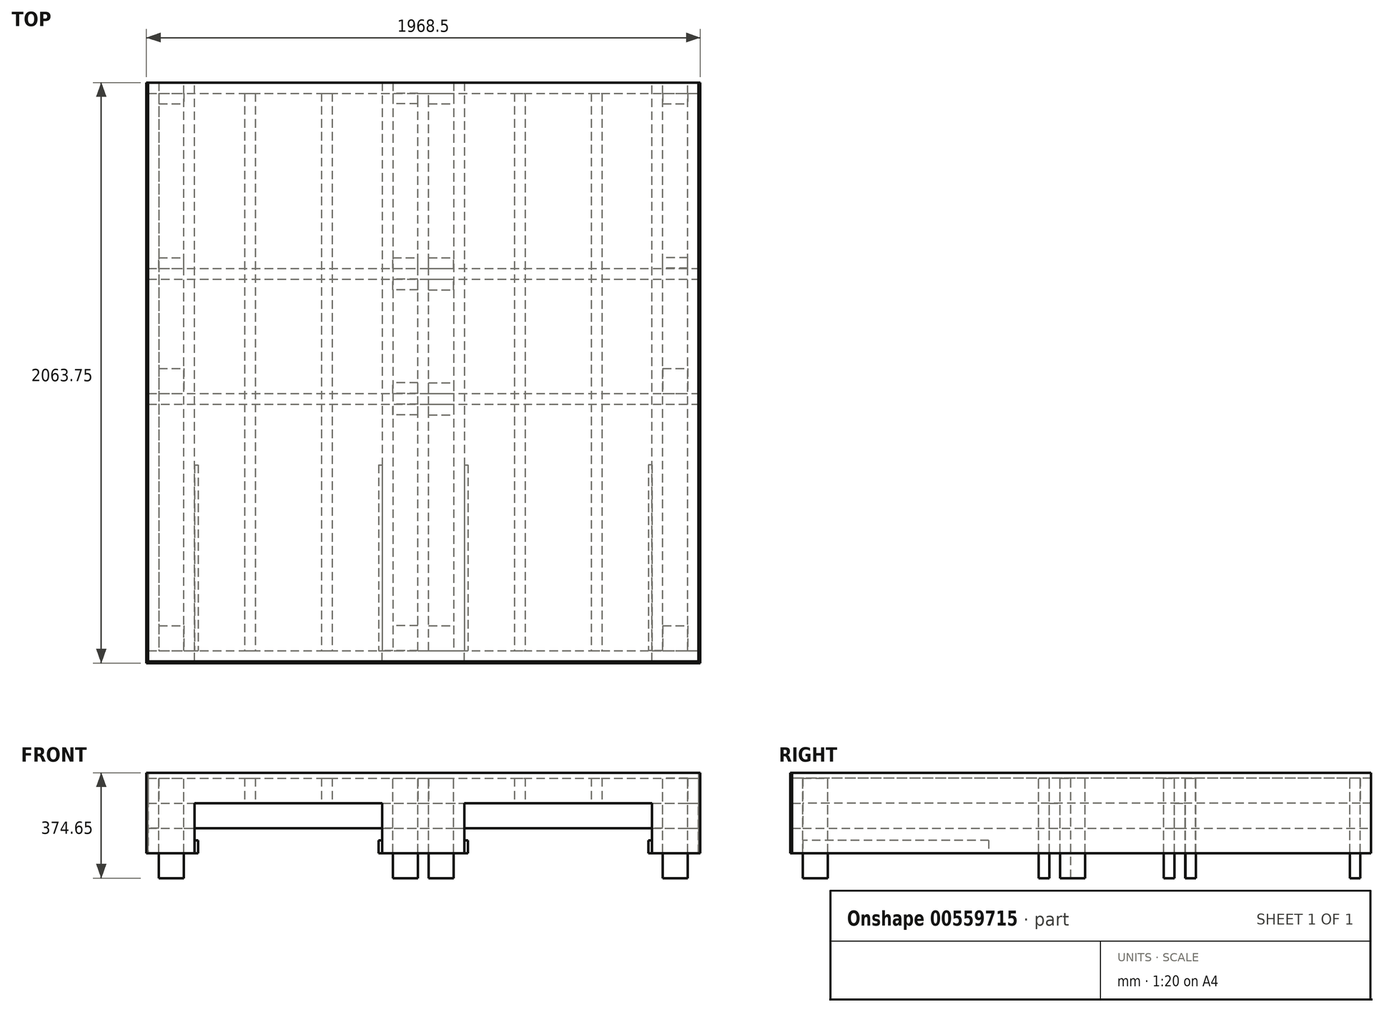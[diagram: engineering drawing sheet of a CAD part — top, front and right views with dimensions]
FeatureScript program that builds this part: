
annotation { "Feature Type Name" : "Feature", "Feature Type Description" : "" }
export const myFeature = defineFeature(function(context is Context, id is Id, definition is map)
    precondition{}
    {
        {
            var Q0;
            Q0=qCreatedBy(makeId("Top.planeOp"),FACE);
            var sketch = newSketch(context, id + "F0", { "sketchPlane" : qUnion([Q0])});
            skLineSegment(sketch, "E0.bottom", {"start": v(-977.9, 1981.2) * mm, "end": v(-939.8, 1981.2) * mm});
            skLineSegment(sketch, "E0.top", {"start": v(-977.9, 0) * mm, "end": v(-939.8, 0) * mm});
            skLineSegment(sketch, "E0.left", {"start": v(-977.9, 1981.2) * mm, "end": v(-977.9, 0) * mm});
            skLineSegment(sketch, "E0.right", {"start": v(-939.8, 1981.2) * mm, "end": v(-939.8, 0) * mm});
            skLineSegment(sketch, "E1.bottom", {"start": v(-361.95, 1981.2) * mm, "end": v(-323.85, 1981.2) * mm});
            skLineSegment(sketch, "E1.top", {"start": v(-361.95, 0) * mm, "end": v(-323.85, 0) * mm});
            skLineSegment(sketch, "E1.left", {"start": v(-361.95, 1981.2) * mm, "end": v(-361.95, 0) * mm});
            skLineSegment(sketch, "E1.right", {"start": v(-323.85, 1981.2) * mm, "end": v(-323.85, 0) * mm});
            skLineSegment(sketch, "E2.bottom", {"start": v(-977.9, -38.1) * mm, "end": v(977.9, -38.1) * mm, "construction": true});
            skLineSegment(sketch, "E2.top", {"start": v(-977.9, 2019.3) * mm, "end": v(977.9, 2019.3) * mm, "construction": true});
            skLineSegment(sketch, "E2.left", {"start": v(-977.9, -38.1) * mm, "end": v(-977.9, 2019.3) * mm, "construction": true});
            skLineSegment(sketch, "E2.right", {"start": v(977.9, -38.1) * mm, "end": v(977.9, 2019.3) * mm, "construction": true});
            skLineSegment(sketch, "E3", {"start": v(0, -38.1) * mm, "end": v(0, 0) * mm, "construction": true});
            skLineSegment(sketch, "E4.bottom", {"start": v(-635, 1981.2) * mm, "end": v(-596.9, 1981.2) * mm});
            skLineSegment(sketch, "E4.top", {"start": v(-635, 0) * mm, "end": v(-596.9, 0) * mm});
            skLineSegment(sketch, "E4.left", {"start": v(-635, 1981.2) * mm, "end": v(-635, 0) * mm});
            skLineSegment(sketch, "E4.right", {"start": v(-596.9, 1981.2) * mm, "end": v(-596.9, 0) * mm});
            skLineSegment(sketch, "E5.bottom", {"start": v(323.85, 1981.2) * mm, "end": v(361.95, 1981.2) * mm});
            skLineSegment(sketch, "E5.top", {"start": v(323.85, 0) * mm, "end": v(361.95, 0) * mm});
            skLineSegment(sketch, "E5.left", {"start": v(323.85, 1981.2) * mm, "end": v(323.85, 0) * mm});
            skLineSegment(sketch, "E5.right", {"start": v(361.95, 1981.2) * mm, "end": v(361.95, 0) * mm});
            skLineSegment(sketch, "E6.bottom", {"start": v(596.9, 1981.2) * mm, "end": v(635, 1981.2) * mm});
            skLineSegment(sketch, "E6.top", {"start": v(596.9, 0) * mm, "end": v(635, 0) * mm});
            skLineSegment(sketch, "E6.left", {"start": v(596.9, 1981.2) * mm, "end": v(596.9, 0) * mm});
            skLineSegment(sketch, "E6.right", {"start": v(635, 1981.2) * mm, "end": v(635, 0) * mm});
            skLineSegment(sketch, "E7.bottom", {"start": v(939.8, 0) * mm, "end": v(977.9, 0) * mm});
            skLineSegment(sketch, "E7.top", {"start": v(939.8, 1981.2) * mm, "end": v(977.9, 1981.2) * mm});
            skLineSegment(sketch, "E7.left", {"start": v(939.8, 0) * mm, "end": v(939.8, 1981.2) * mm});
            skLineSegment(sketch, "E7.right", {"start": v(977.9, 0) * mm, "end": v(977.9, 1981.2) * mm});
            skLineSegment(sketch, "E8.bottom", {"start": v(-19.05, 0) * mm, "end": v(19.05, 0) * mm});
            skLineSegment(sketch, "E8.top", {"start": v(-19.05, 1981.2) * mm, "end": v(19.05, 1981.2) * mm});
            skLineSegment(sketch, "E8.left", {"start": v(-19.05, 0) * mm, "end": v(-19.05, 1981.2) * mm});
            skLineSegment(sketch, "E8.right", {"start": v(19.05, 0) * mm, "end": v(19.05, 1981.2) * mm});
            skSolve(sketch);
        }
        {
            var Q0;
            Q0 = qSketchRegion(id + "F0", true);
            extrude(context, id + "F1", {"entities" : qUnion([Q0]), "depth" : 88.9 * mm, "offsetDistance" : 25.4 * mm});
        }
        {
            var Q0;
            Q0=qCreatedBy(makeId("Top.planeOp"),FACE);
            var sketch = newSketch(context, id + "F2", { "sketchPlane" : qUnion([Q0])});
            skLineSegment(sketch, "E9", {"start": v(-977.9, 1981.2) * mm, "end": v(977.9, 1981.2) * mm});
            skLineSegment(sketch, "E10", {"start": v(977.9, 2019.3) * mm, "end": v(-977.9, 2019.3) * mm});
            skLineSegment(sketch, "E11", {"start": v(-977.9, 2019.3) * mm, "end": v(-977.9, 1981.2) * mm});
            skLineSegment(sketch, "E12", {"start": v(977.9, 2019.3) * mm, "end": v(977.9, 1981.2) * mm});
            skLineSegment(sketch, "E13.bottom", {"start": v(-977.9, 0) * mm, "end": v(977.9, 0) * mm});
            skLineSegment(sketch, "E13.top", {"start": v(-977.9, -38.1) * mm, "end": v(977.9, -38.1) * mm});
            skLineSegment(sketch, "E13.left", {"start": v(-977.9, 0) * mm, "end": v(-977.9, -38.1) * mm});
            skLineSegment(sketch, "E13.right", {"start": v(977.9, 0) * mm, "end": v(977.9, -38.1) * mm});
            skSolve(sketch);
        }
        {
            var Q0;
            Q0 = qSketchRegion(id + "F2", true);
            extrude(context, id + "F3", {"entities" : qUnion([Q0]), "depth" : 88.9 * mm, "offsetDistance" : 25.4 * mm});
        }
        {
            var Q0;
            Q0=makeQuery(id+"F1.opExtrude","CAP_FACE",FACE,{"disambiguationData":[OSD([sQuery(id+"F0.wireOp",EDGE,"E8.bottom"),sQuery(id+"F0.wireOp",EDGE,"E8.top"),sQuery(id+"F0.wireOp",EDGE,"E8.left"),sQuery(id+"F0.wireOp",EDGE,"E8.right")])],"isStart":true});
            var sketch = newSketch(context, id + "F4", { "sketchPlane" : qUnion([Q0])});
            skLineSegment(sketch, "E14.bottom", {"start": v(-977.9, -1320.8) * mm, "end": v(977.9, -1320.8) * mm});
            skLineSegment(sketch, "E14.top", {"start": v(-977.9, -1358.9) * mm, "end": v(977.9, -1358.9) * mm});
            skLineSegment(sketch, "E14.left", {"start": v(-977.9, -1320.8) * mm, "end": v(-977.9, -1358.9) * mm});
            skLineSegment(sketch, "E14.right", {"start": v(977.9, -1320.8) * mm, "end": v(977.9, -1358.9) * mm});
            skLineSegment(sketch, "E15.bottom", {"start": v(-977.9, -876.3) * mm, "end": v(977.9, -876.3) * mm});
            skLineSegment(sketch, "E15.top", {"start": v(-977.9, -914.4) * mm, "end": v(977.9, -914.4) * mm});
            skLineSegment(sketch, "E15.left", {"start": v(-977.9, -876.3) * mm, "end": v(-977.9, -914.4) * mm});
            skLineSegment(sketch, "E15.right", {"start": v(977.9, -876.3) * mm, "end": v(977.9, -914.4) * mm});
            skSolve(sketch);
        }
        {
            var Q0;
            {var subQ0=sQuery(id+"F4.wireOp",EDGE,"E15.left");Q0=makeQuery(id+"F4.imprint","IMPRINT",FACE,{"disambiguationData":[TD([[makeQuery(id+"F4.imprint","IMPRINT",EDGE,{"derivedFrom":subQ0}),1.0]])]});}
            var Q1;
            {var subQ0=sQuery(id+"F4.wireOp",EDGE,"E15.right");Q1=makeQuery(id+"F4.imprint","IMPRINT",FACE,{"disambiguationData":[TD([[makeQuery(id+"F4.imprint","IMPRINT",EDGE,{"derivedFrom":subQ0}),-1.0]])]});}
            var Q2;
            {var subQ0=sQuery(id+"F4.wireOp",EDGE,"E15.bottom");var subQ1=makeQuery(id+"F1.opExtrude","CAP_EDGE",EDGE,{"disambiguationData":[OSD([sQuery(id+"F0.wireOp",EDGE,"EOnk5vKz-xtCF-gDsL-ThLK-PX9BwlTTrQQP.left")])],"isStart":true});var subQ2=makeQuery(id+"F4.imprint","INTERSECT",VERTEX,{"derivedFrom":[subQ1,subQ0]});Q2=makeQuery(id+"F4.imprint","IMPRINT",FACE,{"disambiguationData":[TD([[makeQuery(id+"F4.imprint","IMPRINT",EDGE,{"disambiguationData":[TD([[subQ2,-1.0]])],"derivedFrom":subQ0}),-1.0]])]});}
            var Q3;
            {var subQ0=sQuery(id+"F4.wireOp",EDGE,"E14.right");Q3=makeQuery(id+"F4.imprint","IMPRINT",FACE,{"disambiguationData":[TD([[makeQuery(id+"F4.imprint","IMPRINT",EDGE,{"derivedFrom":subQ0}),-1.0]])]});}
            var Q4;
            {var subQ0=sQuery(id+"F4.wireOp",EDGE,"E14.bottom");var subQ1=makeQuery(id+"F1.opExtrude","CAP_EDGE",EDGE,{"disambiguationData":[OSD([sQuery(id+"F0.wireOp",EDGE,"EOnk5vKz-xtCF-gDsL-ThLK-PX9BwlTTrQQP.left")])],"isStart":true});var subQ2=makeQuery(id+"F4.imprint","INTERSECT",VERTEX,{"derivedFrom":[subQ1,subQ0]});Q4=makeQuery(id+"F4.imprint","IMPRINT",FACE,{"disambiguationData":[TD([[makeQuery(id+"F4.imprint","IMPRINT",EDGE,{"disambiguationData":[TD([[subQ2,-1.0]])],"derivedFrom":subQ0}),-1.0]])]});}
            var Q5;
            {var subQ0=sQuery(id+"F4.wireOp",EDGE,"E14.left");Q5=makeQuery(id+"F4.imprint","IMPRINT",FACE,{"disambiguationData":[TD([[makeQuery(id+"F4.imprint","IMPRINT",EDGE,{"derivedFrom":subQ0}),1.0]])]});}
            extrude(context, id + "F5", {"entities" : qUnion([Q0, Q1, Q2, Q3, Q4, Q5]), "depth" : 88.9 * mm, "offsetDistance" : 25.4 * mm});
        }
        {
            var Q0;
            Q0=makeQuery(id+"F1.opExtrude","CAP_FACE",FACE,{"disambiguationData":[OSD([sQuery(id+"F0.wireOp",EDGE,"E8.bottom"),sQuery(id+"F0.wireOp",EDGE,"E8.top"),sQuery(id+"F0.wireOp",EDGE,"E8.left"),sQuery(id+"F0.wireOp",EDGE,"E8.right")])],"isStart":false});
            var sketch = newSketch(context, id + "F6", { "sketchPlane" : qUnion([Q0])});
            skLineSegment(sketch, "E16.bottom", {"start": v(850.9, 88.9) * mm, "end": v(939.8, 88.9) * mm});
            skLineSegment(sketch, "E16.top", {"start": v(850.9, 0) * mm, "end": v(939.8, 0) * mm});
            skLineSegment(sketch, "E16.left", {"start": v(850.9, 88.9) * mm, "end": v(850.9, 0) * mm});
            skLineSegment(sketch, "E16.right", {"start": v(939.8, 88.9) * mm, "end": v(939.8, 0) * mm});
            skLineSegment(sketch, "E17.bottom", {"start": v(-939.8, 88.9) * mm, "end": v(-850.9, 88.9) * mm});
            skLineSegment(sketch, "E17.top", {"start": v(-939.8, 0) * mm, "end": v(-850.9, 0) * mm});
            skLineSegment(sketch, "E17.left", {"start": v(-939.8, 88.9) * mm, "end": v(-939.8, 0) * mm});
            skLineSegment(sketch, "E17.right", {"start": v(-850.9, 88.9) * mm, "end": v(-850.9, 0) * mm});
            skLineSegment(sketch, "E18.bottom", {"start": v(850.9, 1003.3) * mm, "end": v(939.8, 1003.3) * mm});
            skLineSegment(sketch, "E18.top", {"start": v(850.9, 914.4) * mm, "end": v(939.8, 914.4) * mm});
            skLineSegment(sketch, "E18.left", {"start": v(850.9, 1003.3) * mm, "end": v(850.9, 914.4) * mm});
            skLineSegment(sketch, "E18.right", {"start": v(939.8, 1003.3) * mm, "end": v(939.8, 914.4) * mm});
            skLineSegment(sketch, "E19.bottom", {"start": v(-939.8, 1003.3) * mm, "end": v(-850.9, 1003.3) * mm});
            skLineSegment(sketch, "E19.top", {"start": v(-939.8, 914.4) * mm, "end": v(-850.9, 914.4) * mm});
            skLineSegment(sketch, "E19.left", {"start": v(-939.8, 1003.3) * mm, "end": v(-939.8, 914.4) * mm});
            skLineSegment(sketch, "E19.right", {"start": v(-850.9, 1003.3) * mm, "end": v(-850.9, 914.4) * mm});
            skLineSegment(sketch, "E20.bottom", {"start": v(-19.05, 838.2) * mm, "end": v(-107.95, 838.2) * mm});
            skLineSegment(sketch, "E20.top", {"start": v(-19.05, 876.3) * mm, "end": v(-107.95, 876.3) * mm});
            skLineSegment(sketch, "E20.left", {"start": v(-19.05, 838.2) * mm, "end": v(-19.05, 876.3) * mm});
            skLineSegment(sketch, "E20.right", {"start": v(-107.95, 838.2) * mm, "end": v(-107.95, 876.3) * mm});
            skLineSegment(sketch, "E21.bottom", {"start": v(-19.05, 914.4) * mm, "end": v(-107.95, 914.4) * mm});
            skLineSegment(sketch, "E21.top", {"start": v(-19.05, 952.5) * mm, "end": v(-107.95, 952.5) * mm});
            skLineSegment(sketch, "E21.left", {"start": v(-19.05, 914.4) * mm, "end": v(-19.05, 952.5) * mm});
            skLineSegment(sketch, "E21.right", {"start": v(-107.95, 914.4) * mm, "end": v(-107.95, 952.5) * mm});
            skLineSegment(sketch, "E22.bottom", {"start": v(19.05, 1320.8) * mm, "end": v(107.95, 1320.8) * mm});
            skLineSegment(sketch, "E22.left", {"start": v(19.05, 1320.8) * mm, "end": v(19.05, 1282.7) * mm});
            skLineSegment(sketch, "E23.bottom", {"start": v(-19.05, 1282.7) * mm, "end": v(-107.95, 1282.7) * mm});
            skLineSegment(sketch, "E23.top", {"start": v(-19.05, 1320.8) * mm, "end": v(-107.95, 1320.8) * mm});
            skLineSegment(sketch, "E23.left", {"start": v(-19.05, 1282.7) * mm, "end": v(-19.05, 1320.8) * mm});
            skLineSegment(sketch, "E23.right", {"start": v(-107.95, 1282.7) * mm, "end": v(-107.95, 1320.8) * mm});
            skLineSegment(sketch, "E24.bottom", {"start": v(19.05, 1358.9) * mm, "end": v(107.95, 1358.9) * mm});
            skLineSegment(sketch, "E24.top", {"start": v(19.05, 1397) * mm, "end": v(107.95, 1397) * mm});
            skLineSegment(sketch, "E24.left", {"start": v(19.05, 1358.9) * mm, "end": v(19.05, 1397) * mm});
            skLineSegment(sketch, "E24.right", {"start": v(107.95, 1358.9) * mm, "end": v(107.95, 1397) * mm});
            skPoint(sketch, "E25.oppositeSnap0", {"position": v(63.5, 1397) * mm});
            skLineSegment(sketch, "E25.bottom", {"start": v(939.8, 1359.8) * mm, "end": v(850.9, 1359.8) * mm});
            skLineSegment(sketch, "E25.top", {"start": v(939.8, 1397) * mm, "end": v(850.9, 1397) * mm});
            skLineSegment(sketch, "E25.left", {"start": v(939.8, 1359.8) * mm, "end": v(939.8, 1397) * mm});
            skLineSegment(sketch, "E25.right", {"start": v(850.9, 1359.8) * mm, "end": v(850.9, 1397) * mm});
            skLineSegment(sketch, "E26.bottom", {"start": v(-939.8, 1358.9) * mm, "end": v(-850.9, 1358.9) * mm});
            skLineSegment(sketch, "E26.top", {"start": v(-939.8, 1396.1) * mm, "end": v(-850.9, 1396.1) * mm});
            skLineSegment(sketch, "E26.left", {"start": v(-939.8, 1358.9) * mm, "end": v(-939.8, 1396.1) * mm});
            skLineSegment(sketch, "E26.right", {"start": v(-850.9, 1358.9) * mm, "end": v(-850.9, 1396.1) * mm});
            skLineSegment(sketch, "E27.bottom", {"start": v(-939.8, 1981.2) * mm, "end": v(-850.9, 1981.2) * mm});
            skLineSegment(sketch, "E27.top", {"start": v(-939.8, 1944) * mm, "end": v(-850.9, 1944) * mm});
            skLineSegment(sketch, "E27.left", {"start": v(-939.8, 1981.2) * mm, "end": v(-939.8, 1944) * mm});
            skLineSegment(sketch, "E27.right", {"start": v(-850.9, 1981.2) * mm, "end": v(-850.9, 1944) * mm});
            skLineSegment(sketch, "E28.bottom", {"start": v(850.9, 1981.2) * mm, "end": v(939.8, 1981.2) * mm});
            skLineSegment(sketch, "E28.top", {"start": v(850.9, 1944) * mm, "end": v(939.8, 1944) * mm});
            skLineSegment(sketch, "E28.left", {"start": v(850.9, 1981.2) * mm, "end": v(850.9, 1944) * mm});
            skLineSegment(sketch, "E28.right", {"start": v(939.8, 1981.2) * mm, "end": v(939.8, 1944) * mm});
            skLineSegment(sketch, "E29", {"start": v(19.05, 1282.7) * mm, "end": v(107.95, 1282.7) * mm});
            skLineSegment(sketch, "E30", {"start": v(107.95, 1282.7) * mm, "end": v(107.95, 1320.8) * mm});
            skLineSegment(sketch, "E31.bottom", {"start": v(19.05, 88.9) * mm, "end": v(107.95, 88.9) * mm});
            skLineSegment(sketch, "E31.top", {"start": v(19.05, 0) * mm, "end": v(107.95, 0) * mm});
            skLineSegment(sketch, "E31.left", {"start": v(19.05, 88.9) * mm, "end": v(19.05, 0) * mm});
            skLineSegment(sketch, "E31.right", {"start": v(107.95, 88.9) * mm, "end": v(107.95, 0) * mm});
            skLineSegment(sketch, "E32.bottom", {"start": v(-19.05, 88.9) * mm, "end": v(-107.95, 88.9) * mm});
            skLineSegment(sketch, "E32.top", {"start": v(-19.05, 0) * mm, "end": v(-107.95, 0) * mm});
            skLineSegment(sketch, "E32.left", {"start": v(-19.05, 88.9) * mm, "end": v(-19.05, 0) * mm});
            skLineSegment(sketch, "E32.right", {"start": v(-107.95, 88.9) * mm, "end": v(-107.95, 0) * mm});
            skPoint(sketch, "E33.firstSnap0", {"position": v(63.5, 1358.9) * mm});
            skLineSegment(sketch, "E33.bottom", {"start": v(-107.95, 1358.9) * mm, "end": v(-19.05, 1358.9) * mm});
            skLineSegment(sketch, "E33.top", {"start": v(-107.95, 1397) * mm, "end": v(-19.05, 1397) * mm});
            skLineSegment(sketch, "E33.left", {"start": v(-107.95, 1358.9) * mm, "end": v(-107.95, 1397) * mm});
            skLineSegment(sketch, "E33.right", {"start": v(-19.05, 1358.9) * mm, "end": v(-19.05, 1397) * mm});
            skLineSegment(sketch, "E34.bottom", {"start": v(19.05, 876.3) * mm, "end": v(107.95, 876.3) * mm});
            skLineSegment(sketch, "E34.top", {"start": v(19.05, 838.2) * mm, "end": v(107.95, 838.2) * mm});
            skLineSegment(sketch, "E34.left", {"start": v(19.05, 876.3) * mm, "end": v(19.05, 838.2) * mm});
            skLineSegment(sketch, "E34.right", {"start": v(107.95, 876.3) * mm, "end": v(107.95, 838.2) * mm});
            skLineSegment(sketch, "E35.bottom", {"start": v(19.05, 952.5) * mm, "end": v(107.95, 952.5) * mm});
            skLineSegment(sketch, "E35.top", {"start": v(19.05, 914.4) * mm, "end": v(107.95, 914.4) * mm});
            skLineSegment(sketch, "E35.left", {"start": v(19.05, 952.5) * mm, "end": v(19.05, 914.4) * mm});
            skLineSegment(sketch, "E35.right", {"start": v(107.95, 952.5) * mm, "end": v(107.95, 914.4) * mm});
            skLineSegment(sketch, "E36.bottom", {"start": v(19.05, 1981.2) * mm, "end": v(107.95, 1981.2) * mm});
            skLineSegment(sketch, "E36.top", {"start": v(19.05, 1944) * mm, "end": v(107.95, 1944) * mm});
            skLineSegment(sketch, "E36.left", {"start": v(19.05, 1981.2) * mm, "end": v(19.05, 1944) * mm});
            skLineSegment(sketch, "E36.right", {"start": v(107.95, 1981.2) * mm, "end": v(107.95, 1944) * mm});
            skLineSegment(sketch, "E37.bottom", {"start": v(-19.05, 1981.2) * mm, "end": v(-107.95, 1981.2) * mm});
            skLineSegment(sketch, "E37.top", {"start": v(-19.05, 1944) * mm, "end": v(-107.95, 1944) * mm});
            skLineSegment(sketch, "E37.left", {"start": v(-19.05, 1981.2) * mm, "end": v(-19.05, 1944) * mm});
            skLineSegment(sketch, "E37.right", {"start": v(-107.95, 1981.2) * mm, "end": v(-107.95, 1944) * mm});
            skSolve(sketch);
        }
        {
            var Q0;
            Q0 = qSketchRegion(id + "F6", true);
            extrude(context, id + "F7", {"entities" : qUnion([Q0]), "oppositeDirection" : true, "depth" : 355.6 * mm, "offsetDistance" : 25.4 * mm});
        }
        {
            var Q0;
            Q0=makeQuery(id+"F5.opExtrude","CAP_FACE",FACE,{"disambiguationData":[OSD([sQuery(id+"F4.wireOp",EDGE,"E15.bottom"),sQuery(id+"F4.wireOp",EDGE,"E15.top"),sQuery(id+"F4.wireOp",EDGE,"E15.left"),sQuery(id+"F4.wireOp",EDGE,"E15.right")])],"isStart":false});
            var sketch = newSketch(context, id + "F8", { "sketchPlane" : qUnion([Q0])});
            skLineSegment(sketch, "E38.bottom", {"start": v(850.9, 0) * mm, "end": v(812.8, 0) * mm});
            skLineSegment(sketch, "E38.top", {"start": v(850.9, -2019.3) * mm, "end": v(812.8, -2019.3) * mm});
            skLineSegment(sketch, "E38.left", {"start": v(850.9, 0) * mm, "end": v(850.9, -2019.3) * mm});
            skLineSegment(sketch, "E38.right", {"start": v(812.8, 0) * mm, "end": v(812.8, -2019.3) * mm});
            skLineSegment(sketch, "E39.bottom", {"start": v(-850.9, 0) * mm, "end": v(-812.8, 0) * mm});
            skLineSegment(sketch, "E39.top", {"start": v(-850.9, -2019.3) * mm, "end": v(-812.8, -2019.3) * mm});
            skLineSegment(sketch, "E39.left", {"start": v(-850.9, 0) * mm, "end": v(-850.9, -2019.3) * mm});
            skLineSegment(sketch, "E39.right", {"start": v(-812.8, 0) * mm, "end": v(-812.8, -2019.3) * mm});
            skLineSegment(sketch, "E40.bottom", {"start": v(107.95, -2019.3) * mm, "end": v(146.05, -2019.3) * mm});
            skLineSegment(sketch, "E40.top", {"start": v(107.95, 0) * mm, "end": v(146.05, 0) * mm});
            skLineSegment(sketch, "E40.left", {"start": v(107.95, -2019.3) * mm, "end": v(107.95, 0) * mm});
            skLineSegment(sketch, "E40.right", {"start": v(146.05, -2019.3) * mm, "end": v(146.05, 0) * mm});
            skLineSegment(sketch, "E41.bottom", {"start": v(-107.95, -2019.3) * mm, "end": v(-146.05, -2019.3) * mm});
            skLineSegment(sketch, "E41.top", {"start": v(-107.95, 0) * mm, "end": v(-146.05, 0) * mm});
            skLineSegment(sketch, "E41.left", {"start": v(-107.95, -2019.3) * mm, "end": v(-107.95, 0) * mm});
            skLineSegment(sketch, "E41.right", {"start": v(-146.05, -2019.3) * mm, "end": v(-146.05, 0) * mm});
            skLineSegment(sketch, "E42.bottom", {"start": v(939.8, 0) * mm, "end": v(977.9, 0) * mm});
            skLineSegment(sketch, "E42.top", {"start": v(939.8, -2019.3) * mm, "end": v(977.9, -2019.3) * mm});
            skLineSegment(sketch, "E42.left", {"start": v(939.8, 0) * mm, "end": v(939.8, -2019.3) * mm});
            skLineSegment(sketch, "E42.right", {"start": v(977.9, 0) * mm, "end": v(977.9, -2019.3) * mm});
            skLineSegment(sketch, "E43.bottom", {"start": v(-939.8, -2019.3) * mm, "end": v(-977.9, -2019.3) * mm});
            skLineSegment(sketch, "E43.top", {"start": v(-939.8, 0) * mm, "end": v(-977.9, 0) * mm});
            skLineSegment(sketch, "E43.left", {"start": v(-939.8, -2019.3) * mm, "end": v(-939.8, 0) * mm});
            skLineSegment(sketch, "E43.right", {"start": v(-977.9, -2019.3) * mm, "end": v(-977.9, 0) * mm});
            skSolve(sketch);
        }
        {
            var Q0;
            Q0 = qSketchRegion(id + "F8", true);
            extrude(context, id + "F9", {"entities" : qUnion([Q0]), "depth" : 88.9 * mm, "offsetDistance" : 25.4 * mm});
        }
        {
            var Q0;
            Q0=qCreatedBy(makeId("Front.planeOp"),FACE);
            var sketch = newSketch(context, id + "F10", { "sketchPlane" : qUnion([Q0])});
            skLineSegment(sketch, "E44.bottom", {"start": v(146.05, -132.08) * mm, "end": v(158.75, -132.08) * mm});
            skLineSegment(sketch, "E44.top", {"start": v(146.05, -177.8) * mm, "end": v(158.75, -177.8) * mm});
            skLineSegment(sketch, "E44.left", {"start": v(146.05, -132.08) * mm, "end": v(146.05, -177.8) * mm});
            skLineSegment(sketch, "E44.right", {"start": v(158.75, -132.08) * mm, "end": v(158.75, -177.8) * mm});
            skLineSegment(sketch, "E45.bottom", {"start": v(-158.75, -132.08) * mm, "end": v(-146.05, -132.08) * mm});
            skLineSegment(sketch, "E45.top", {"start": v(-158.75, -177.8) * mm, "end": v(-146.05, -177.8) * mm});
            skLineSegment(sketch, "E45.left", {"start": v(-158.75, -132.08) * mm, "end": v(-158.75, -177.8) * mm});
            skLineSegment(sketch, "E45.right", {"start": v(-146.05, -132.08) * mm, "end": v(-146.05, -177.8) * mm});
            skLineSegment(sketch, "E46.bottom", {"start": v(812.8, -177.8) * mm, "end": v(800.1, -177.8) * mm});
            skLineSegment(sketch, "E46.top", {"start": v(812.8, -132.08) * mm, "end": v(800.1, -132.08) * mm});
            skLineSegment(sketch, "E46.left", {"start": v(812.8, -177.8) * mm, "end": v(812.8, -132.08) * mm});
            skLineSegment(sketch, "E46.right", {"start": v(800.1, -177.8) * mm, "end": v(800.1, -132.08) * mm});
            skLineSegment(sketch, "E47.bottom", {"start": v(-812.8, -177.8) * mm, "end": v(-800.1, -177.8) * mm});
            skLineSegment(sketch, "E47.top", {"start": v(-812.8, -132.08) * mm, "end": v(-800.1, -132.08) * mm});
            skLineSegment(sketch, "E47.left", {"start": v(-812.8, -177.8) * mm, "end": v(-812.8, -132.08) * mm});
            skLineSegment(sketch, "E47.right", {"start": v(-800.1, -177.8) * mm, "end": v(-800.1, -132.08) * mm});
            skSolve(sketch);
        }
        {
            var Q0;
            Q0 = qSketchRegion(id + "F10", true);
            extrude(context, id + "F11", {"entities" : qUnion([Q0]), "oppositeDirection" : true, "depth" : 660.4 * mm, "offsetDistance" : 25.4 * mm});
        }
        {
            var Q0;
            Q0=qCreatedBy(makeId("Front.planeOp"),FACE);
            var sketch = newSketch(context, id + "F12", { "sketchPlane" : qUnion([Q0])});
            skLineSegment(sketch, "E48.bottom", {"start": v(977.9, -177.8) * mm, "end": v(812.8, -177.8) * mm});
            skLineSegment(sketch, "E48.top", {"start": v(977.9, -88.9) * mm, "end": v(812.8, -88.9) * mm});
            skLineSegment(sketch, "E48.left", {"start": v(977.9, -177.8) * mm, "end": v(977.9, -88.9) * mm});
            skLineSegment(sketch, "E48.right", {"start": v(812.8, -177.8) * mm, "end": v(812.8, -88.9) * mm});
            skLineSegment(sketch, "E49.bottom", {"start": v(-146.05, -88.9) * mm, "end": v(146.05, -88.9) * mm});
            skLineSegment(sketch, "E49.top", {"start": v(-146.05, -177.8) * mm, "end": v(146.05, -177.8) * mm});
            skLineSegment(sketch, "E49.left", {"start": v(-146.05, -88.9) * mm, "end": v(-146.05, -177.8) * mm});
            skLineSegment(sketch, "E49.right", {"start": v(146.05, -88.9) * mm, "end": v(146.05, -177.8) * mm});
            skLineSegment(sketch, "E50.bottom", {"start": v(-977.9, -88.9) * mm, "end": v(-812.8, -88.9) * mm});
            skLineSegment(sketch, "E50.top", {"start": v(-977.9, -177.8) * mm, "end": v(-812.8, -177.8) * mm});
            skLineSegment(sketch, "E50.left", {"start": v(-977.9, -88.9) * mm, "end": v(-977.9, -177.8) * mm});
            skLineSegment(sketch, "E50.right", {"start": v(-812.8, -88.9) * mm, "end": v(-812.8, -177.8) * mm});
            skSolve(sketch);
        }
        {
            var Q0;
            Q0 = qSketchRegion(id + "F12", true);
            extrude(context, id + "F13", {"entities" : qUnion([Q0]), "depth" : 38.1 * mm, "offsetDistance" : 25.4 * mm});
        }
        {
            var Q0;
            Q0=makeQuery(id+"F3.opExtrude","CAP_FACE",FACE,{"disambiguationData":[OSD([sQuery(id+"F2.wireOp",EDGE,"E13.bottom"),sQuery(id+"F2.wireOp",EDGE,"E13.top"),sQuery(id+"F2.wireOp",EDGE,"E13.left"),sQuery(id+"F2.wireOp",EDGE,"E13.right")])],"isStart":false});
            var sketch = newSketch(context, id + "F14", { "sketchPlane" : qUnion([Q0])});
            skLineSegment(sketch, "E51.bottom", {"start": v(-977.9, 2019.3) * mm, "end": v(977.9, 2019.3) * mm});
            skLineSegment(sketch, "E51.top", {"start": v(-977.9, -38.1) * mm, "end": v(977.9, -38.1) * mm});
            skLineSegment(sketch, "E51.left", {"start": v(-977.9, 2019.3) * mm, "end": v(-977.9, -38.1) * mm});
            skLineSegment(sketch, "E51.right", {"start": v(977.9, 2019.3) * mm, "end": v(977.9, -38.1) * mm});
            skSolve(sketch);
        }
        {
            var Q0;
            Q0 = qSketchRegion(id + "F14", true);
            extrude(context, id + "F15", {"entities" : qUnion([Q0]), "depth" : 19.05 * mm, "offsetDistance" : 25.4 * mm});
        }
        {
            var Q0;
            Q0=makeQuery(id+"F1.opExtrude","SWEPT_FACE",FACE,{"disambiguationData":[OSD([sQuery(id+"F0.wireOp",EDGE,"E7.right")])]});
            var sketch = newSketch(context, id + "F16", { "sketchPlane" : qUnion([Q0])});
            skLineSegment(sketch, "E52.bottom", {"start": v(-38.1, 107.95) * mm, "end": v(2019.3, 107.95) * mm});
            skLineSegment(sketch, "E52.top", {"start": v(-38.1, -177.8) * mm, "end": v(2019.3, -177.8) * mm});
            skLineSegment(sketch, "E52.left", {"start": v(-38.1, 107.95) * mm, "end": v(-38.1, -177.8) * mm});
            skLineSegment(sketch, "E52.right", {"start": v(2019.3, 107.95) * mm, "end": v(2019.3, -177.8) * mm});
            skSolve(sketch);
        }
        {
            var Q0;
            Q0 = qSketchRegion(id + "F16", true);
            extrude(context, id + "F17", {"entities" : qUnion([Q0]), "depth" : 6.35 * mm, "offsetDistance" : 25.4 * mm});
        }
        {
            var Q0;
            Q0=makeQuery(id+"F1.opExtrude","SWEPT_FACE",FACE,{"disambiguationData":[OSD([sQuery(id+"F0.wireOp",EDGE,"E0.left")])]});
            var sketch = newSketch(context, id + "F18", { "sketchPlane" : qUnion([Q0])});
            skLineSegment(sketch, "E53.bottom", {"start": v(-2019.3, 107.95) * mm, "end": v(38.1, 107.95) * mm});
            skLineSegment(sketch, "E53.top", {"start": v(-2019.3, -177.8) * mm, "end": v(38.1, -177.8) * mm});
            skLineSegment(sketch, "E53.left", {"start": v(-2019.3, 107.95) * mm, "end": v(-2019.3, -177.8) * mm});
            skLineSegment(sketch, "E53.right", {"start": v(38.1, 107.95) * mm, "end": v(38.1, -177.8) * mm});
            skSolve(sketch);
        }
        {
            var Q0;
            Q0 = qSketchRegion(id + "F18", true);
            extrude(context, id + "F19", {"entities" : qUnion([Q0]), "depth" : 6.35 * mm, "offsetDistance" : 25.4 * mm});
        }
        {
            var Q0;
            Q0=makeQuery(id+"F7.opExtrude","SWEPT_FACE",FACE,{"disambiguationData":[OSD([sQuery(id+"F6.wireOp",EDGE,"E31.top")])]});
            var sketch = newSketch(context, id + "F20", { "sketchPlane" : qUnion([Q0])});
            skLineSegment(sketch, "E54.bottom", {"start": v(-146.05, 0) * mm, "end": v(146.05, 0) * mm});
            skLineSegment(sketch, "E54.top", {"start": v(-146.05, -88.9) * mm, "end": v(146.05, -88.9) * mm});
            skLineSegment(sketch, "E54.left", {"start": v(-146.05, 0) * mm, "end": v(-146.05, -88.9) * mm});
            skLineSegment(sketch, "E54.right", {"start": v(146.05, 0) * mm, "end": v(146.05, -88.9) * mm});
            skLineSegment(sketch, "E55.bottom", {"start": v(812.8, 0) * mm, "end": v(977.9, 0) * mm});
            skLineSegment(sketch, "E55.top", {"start": v(812.8, -88.9) * mm, "end": v(977.9, -88.9) * mm});
            skLineSegment(sketch, "E55.left", {"start": v(812.8, 0) * mm, "end": v(812.8, -88.9) * mm});
            skLineSegment(sketch, "E55.right", {"start": v(977.9, 0) * mm, "end": v(977.9, -88.9) * mm});
            skLineSegment(sketch, "E56.bottom", {"start": v(-977.9, 0) * mm, "end": v(-812.8, 0) * mm});
            skLineSegment(sketch, "E56.top", {"start": v(-977.9, -88.9) * mm, "end": v(-812.8, -88.9) * mm});
            skLineSegment(sketch, "E56.left", {"start": v(-977.9, 0) * mm, "end": v(-977.9, -88.9) * mm});
            skLineSegment(sketch, "E56.right", {"start": v(-812.8, 0) * mm, "end": v(-812.8, -88.9) * mm});
            skSolve(sketch);
        }
        {
            var Q0;
            Q0 = qSketchRegion(id + "F20", true);
            extrude(context, id + "F21", {"entities" : qUnion([Q0]), "depth" : 38.1 * mm, "offsetDistance" : 25.4 * mm});
        }
        {
            var Q0;
            Q0=makeQuery(id+"F3.opExtrude","SWEPT_FACE",FACE,{"disambiguationData":[OSD([sQuery(id+"F2.wireOp",EDGE,"E13.top")])]});
            var sketch = newSketch(context, id + "F22", { "sketchPlane" : qUnion([Q0])});
            skLineSegment(sketch, "E57", {"start": v(-984.25, -177.8) * mm, "end": v(-984.25, 107.95) * mm});
            skLineSegment(sketch, "E58", {"start": v(-984.25, 107.95) * mm, "end": v(984.25, 107.95) * mm});
            skLineSegment(sketch, "E59", {"start": v(984.25, 107.95) * mm, "end": v(984.25, -177.8) * mm});
            skLineSegment(sketch, "E60", {"start": v(984.25, -177.8) * mm, "end": v(812.8, -177.8) * mm});
            skLineSegment(sketch, "E61", {"start": v(812.8, -177.8) * mm, "end": v(812.8, 0) * mm});
            skLineSegment(sketch, "E62", {"start": v(812.8, 0) * mm, "end": v(146.05, 0) * mm});
            skLineSegment(sketch, "E63", {"start": v(146.05, 0) * mm, "end": v(146.05, -177.8) * mm});
            skLineSegment(sketch, "E64", {"start": v(146.05, -177.8) * mm, "end": v(-146.05, -177.8) * mm});
            skLineSegment(sketch, "E65", {"start": v(-146.05, -177.8) * mm, "end": v(-146.05, 0) * mm});
            skLineSegment(sketch, "E66", {"start": v(-146.05, 0) * mm, "end": v(-812.8, 0) * mm});
            skLineSegment(sketch, "E67", {"start": v(-812.8, 0) * mm, "end": v(-812.8, -177.8) * mm});
            skLineSegment(sketch, "E68", {"start": v(-812.8, -177.8) * mm, "end": v(-984.25, -177.8) * mm});
            skSolve(sketch);
        }
        {
            var Q0;
            Q0 = qSketchRegion(id + "F22", true);
            extrude(context, id + "F23", {"entities" : qUnion([Q0]), "depth" : 6.35 * mm, "offsetDistance" : 25.4 * mm});
        }
    });
